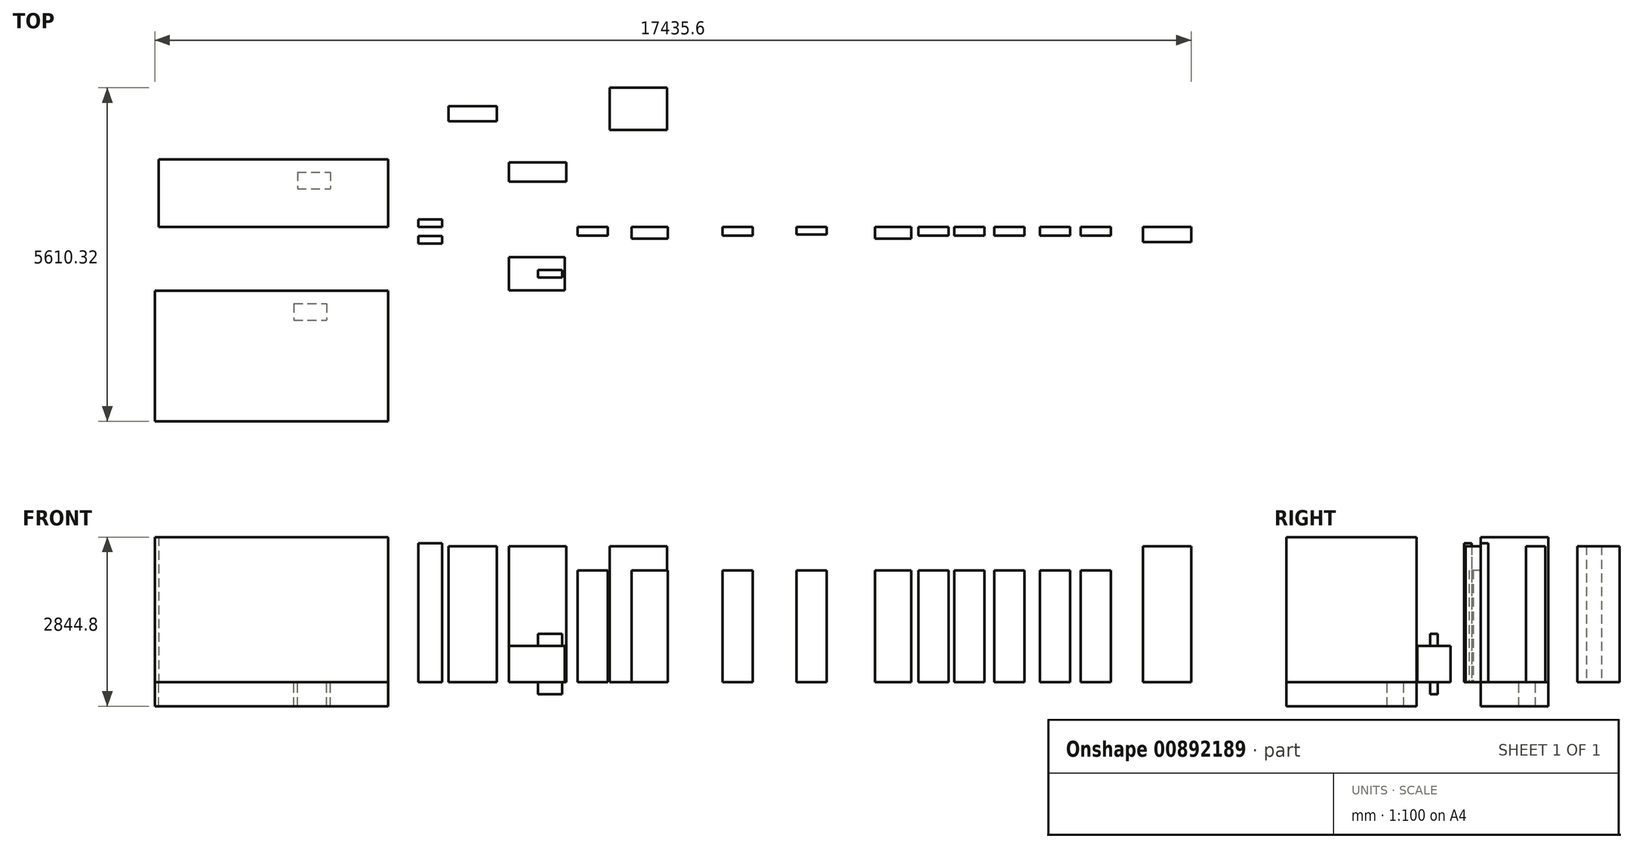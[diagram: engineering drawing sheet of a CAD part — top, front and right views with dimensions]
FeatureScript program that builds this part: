
annotation { "Feature Type Name" : "Feature", "Feature Type Description" : "" }
export const myFeature = defineFeature(function(context is Context, id is Id, definition is map)
    precondition{}
    {
        {
            var Q0;
            Q0=qCreatedBy(makeId("Top.planeOp"),FACE);
            var sketch = newSketch(context, id + "F0", { "sketchPlane" : qUnion([Q0])});
            skLineSegment(sketch, "E0.bottom", {"start": v(0, 0) * mm, "end": v(401.32, 0) * mm});
            skLineSegment(sketch, "E0.top", {"start": v(0, 127) * mm, "end": v(401.32, 127) * mm});
            skLineSegment(sketch, "E0.left", {"start": v(0, 0) * mm, "end": v(0, 127) * mm});
            skLineSegment(sketch, "E0.right", {"start": v(401.32, 0) * mm, "end": v(401.32, 127) * mm});
            skSolve(sketch);
        }
        {
            var Q0;
            Q0=makeQuery(id+"F0.imprint","IMPRINT",FACE,{"disambiguationData":[TD([[makeQuery(id+"F0.imprint","IMPRINT",EDGE,{"derivedFrom":sQuery(id+"F0.wireOp",EDGE,"E0.bottom")}),1.0]])]});
            extrude(context, id + "F1", {"entities" : qUnion([Q0]), "depth" : 2336.8 * mm, "offsetDistance" : 25.4 * mm});
        }
        {
            var Q0;
            Q0=qCreatedBy(makeId("Top.planeOp"),FACE);
            var sketch = newSketch(context, id + "F2", { "sketchPlane" : qUnion([Q0])});
            skLineSegment(sketch, "E1", {"start": v(0, 0) * mm, "end": v(-508, 0) * mm, "construction": true});
            skLineSegment(sketch, "E2.bottom", {"start": v(-508, 0) * mm, "end": v(-4369.82, 0) * mm});
            skLineSegment(sketch, "E2.top", {"start": v(-508, 1138.94) * mm, "end": v(-4369.82, 1138.94) * mm});
            skLineSegment(sketch, "E2.left", {"start": v(-508, 0) * mm, "end": v(-508, 1138.94) * mm});
            skLineSegment(sketch, "E2.right", {"start": v(-4369.82, 0) * mm, "end": v(-4369.82, 1138.94) * mm});
            skLineSegment(sketch, "E3", {"start": v(-4369.82, 1138.94) * mm, "end": v(-2033.02, 1138.94) * mm, "construction": true});
            skLineSegment(sketch, "E4", {"start": v(-2033.02, 1138.94) * mm, "end": v(-2033.02, 923.04) * mm, "construction": true});
            skLineSegment(sketch, "E5.bottom", {"start": v(-2033.02, 923.04) * mm, "end": v(-1479.3, 923.04) * mm});
            skLineSegment(sketch, "E5.top", {"start": v(-2033.02, 643.64) * mm, "end": v(-1479.3, 643.64) * mm});
            skLineSegment(sketch, "E5.left", {"start": v(-2033.02, 923.04) * mm, "end": v(-2033.02, 643.64) * mm});
            skLineSegment(sketch, "E5.right", {"start": v(-1479.3, 923.04) * mm, "end": v(-1479.3, 643.64) * mm});
            skSolve(sketch);
        }
        {
            var Q0;
            Q0=makeQuery(id+"F2.imprint","IMPRINT",FACE,{"disambiguationData":[TD([[makeQuery(id+"F2.imprint","IMPRINT",EDGE,{"derivedFrom":sQuery(id+"F2.wireOp",EDGE,"E2.bottom")}),-1.0]])]});
            extrude(context, id + "F3", {"entities" : qUnion([Q0]), "oppositeDirection" : true, "depth" : 406.4 * mm, "offsetDistance" : 25.4 * mm});
        }
        {
            var Q0;
            Q0=qCreatedBy(makeId("Top.planeOp"),FACE);
            var sketch = newSketch(context, id + "F4", { "sketchPlane" : qUnion([Q0])});
            skLineSegment(sketch, "E6", {"start": v(0, 0) * mm, "end": v(0, -1524) * mm, "construction": true});
            skLineSegment(sketch, "E7", {"start": v(0, -1524) * mm, "end": v(-508, -1524) * mm, "construction": true});
            skLineSegment(sketch, "E8", {"start": v(-508, -1524) * mm, "end": v(-508, -3269.23) * mm});
            skLineSegment(sketch, "E9", {"start": v(-508, -3269.23) * mm, "end": v(-4430.78, -3269.23) * mm});
            skLineSegment(sketch, "E10", {"start": v(-4430.78, -3269.23) * mm, "end": v(-4430.78, -1075.7) * mm});
            skLineSegment(sketch, "E11", {"start": v(-4430.78, -1075.7) * mm, "end": v(-2581.4, -1075.7) * mm});
            skLineSegment(sketch, "E12", {"start": v(-4430.78, -1075.7) * mm, "end": v(-2093.98, -1075.7) * mm, "construction": true});
            skLineSegment(sketch, "E13", {"start": v(-2093.98, -1075.7) * mm, "end": v(-2093.98, -1291.6) * mm, "construction": true});
            skLineSegment(sketch, "E14.bottom", {"start": v(-2093.98, -1291.6) * mm, "end": v(-1540.26, -1291.6) * mm});
            skLineSegment(sketch, "E14.top", {"start": v(-2093.98, -1571) * mm, "end": v(-1540.26, -1571) * mm});
            skLineSegment(sketch, "E14.left", {"start": v(-2093.98, -1291.6) * mm, "end": v(-2093.98, -1571) * mm});
            skLineSegment(sketch, "E14.right", {"start": v(-1540.26, -1291.6) * mm, "end": v(-1540.26, -1571) * mm});
            skLineSegment(sketch, "E15", {"start": v(-2581.4, -1075.7) * mm, "end": v(-508, -1075.7) * mm});
            skLineSegment(sketch, "E16", {"start": v(-508, -1075.7) * mm, "end": v(-508, -1524) * mm});
            skSolve(sketch);
        }
        {
            var Q0;
            Q0=makeQuery(id+"F4.imprint","IMPRINT",FACE,{"disambiguationData":[TD([[makeQuery(id+"F4.imprint","IMPRINT",EDGE,{"derivedFrom":sQuery(id+"F4.wireOp",EDGE,"E8")}),-1.0]])]});
            extrude(context, id + "F5", {"entities" : qUnion([Q0]), "oppositeDirection" : true, "depth" : 406.4 * mm, "offsetDistance" : 25.4 * mm});
        }
        {
            var Q0;
            Q0=qCreatedBy(makeId("Top.planeOp"),FACE);
            var sketch = newSketch(context, id + "F6", { "sketchPlane" : qUnion([Q0])});
            skLineSegment(sketch, "E17", {"start": v(0, 0) * mm, "end": v(0, -508) * mm, "construction": true});
            skLineSegment(sketch, "E18", {"start": v(0, -508) * mm, "end": v(1524, -508) * mm, "construction": true});
            skLineSegment(sketch, "E19.bottom", {"start": v(1524, -508) * mm, "end": v(2463.8, -508) * mm});
            skLineSegment(sketch, "E19.top", {"start": v(1524, -1066.8) * mm, "end": v(2463.8, -1066.8) * mm});
            skLineSegment(sketch, "E19.left", {"start": v(1524, -508) * mm, "end": v(1524, -1066.8) * mm});
            skLineSegment(sketch, "E19.right", {"start": v(2463.8, -508) * mm, "end": v(2463.8, -1066.8) * mm});
            skLineSegment(sketch, "E20", {"start": v(2463.8, -508) * mm, "end": v(2217.42, -508) * mm, "construction": true});
            skLineSegment(sketch, "E21", {"start": v(2217.42, -508) * mm, "end": v(2217.42, -787.4) * mm, "construction": true});
            skLineSegment(sketch, "E22.bottom", {"start": v(2418.08, -850.9) * mm, "end": v(2016.76, -850.9) * mm});
            skLineSegment(sketch, "E22.top", {"start": v(2418.08, -723.9) * mm, "end": v(2016.76, -723.9) * mm});
            skLineSegment(sketch, "E22.left", {"start": v(2418.08, -850.9) * mm, "end": v(2418.08, -723.9) * mm});
            skLineSegment(sketch, "E22.right", {"start": v(2016.76, -850.9) * mm, "end": v(2016.76, -723.9) * mm});
            skPoint(sketch, "E22.middle", {"position": v(2217.42, -787.4) * mm});
            skSolve(sketch);
        }
        {
            var Q0;
            Q0=makeQuery(id+"F6.imprint","IMPRINT",FACE,{"disambiguationData":[TD([[makeQuery(id+"F6.imprint","IMPRINT",EDGE,{"derivedFrom":sQuery(id+"F6.wireOp",EDGE,"E19.bottom")}),-1.0]])]});
            var Q1;
            Q1=makeQuery(id+"F6.imprint","IMPRINT",FACE,{"disambiguationData":[TD([[makeQuery(id+"F6.imprint","IMPRINT",EDGE,{"derivedFrom":sQuery(id+"F6.wireOp",EDGE,"E22.bottom")}),-1.0]])]});
            extrude(context, id + "F7", {"entities" : qUnion([Q0, Q1]), "depth" : 609.6 * mm, "offsetDistance" : 25.4 * mm});
        }
        {
            var Q0;
            Q0=makeQuery(id+"F6.imprint","IMPRINT",FACE,{"disambiguationData":[TD([[makeQuery(id+"F6.imprint","IMPRINT",EDGE,{"derivedFrom":sQuery(id+"F6.wireOp",EDGE,"E22.bottom")}),-1.0]])]});
            extrude(context, id + "F8", {"entities" : qUnion([Q0]), "operationType" : NewBodyOperationType.ADD, "oppositeDirection" : true, "depth" : 203.2 * mm, "offsetDistance" : 25.4 * mm});
        }
        {
            var Q0;
            Q0=makeQuery(id+"F7.opExtrude","CAP_FACE",FACE,{"disambiguationData":[OSD([sQuery(id+"F6.wireOp",EDGE,"E19.bottom"),sQuery(id+"F6.wireOp",EDGE,"E19.top"),sQuery(id+"F6.wireOp",EDGE,"E19.left"),sQuery(id+"F6.wireOp",EDGE,"E19.right")])],"isStart":false});
            var sketch = newSketch(context, id + "F9", { "sketchPlane" : qUnion([Q0])});
            skLineSegment(sketch, "E23", {"start": v(2463.8, -787.4) * mm, "end": v(2217.42, -787.4) * mm, "construction": true});
            skLineSegment(sketch, "E24.bottom", {"start": v(2418.08, -850.9) * mm, "end": v(2016.76, -850.9) * mm});
            skLineSegment(sketch, "E24.top", {"start": v(2418.08, -723.9) * mm, "end": v(2016.76, -723.9) * mm});
            skLineSegment(sketch, "E24.left", {"start": v(2418.08, -850.9) * mm, "end": v(2418.08, -723.9) * mm});
            skLineSegment(sketch, "E24.right", {"start": v(2016.76, -850.9) * mm, "end": v(2016.76, -723.9) * mm});
            skPoint(sketch, "E24.middle", {"position": v(2217.42, -787.4) * mm});
            skSolve(sketch);
        }
        {
            var Q0;
            Q0=makeQuery(id+"F9.imprint","IMPRINT",FACE,{"disambiguationData":[TD([[makeQuery(id+"F9.imprint","IMPRINT",EDGE,{"derivedFrom":sQuery(id+"F9.wireOp",EDGE,"E24.bottom")}),-1.0]])]});
            extrude(context, id + "F10", {"entities" : qUnion([Q0]), "operationType" : NewBodyOperationType.ADD, "depth" : 203.2 * mm, "offsetDistance" : 25.4 * mm});
        }
        {
            var Q0;
            Q0=makeQuery(id+"F2.imprint","IMPRINT",FACE,{"disambiguationData":[TD([[makeQuery(id+"F2.imprint","IMPRINT",EDGE,{"derivedFrom":sQuery(id+"F2.wireOp",EDGE,"E2.bottom")}),-1.0]])]});
            var Q1;
            Q1=makeQuery(id+"F2.imprint","IMPRINT",FACE,{"disambiguationData":[TD([[makeQuery(id+"F2.imprint","IMPRINT",EDGE,{"derivedFrom":sQuery(id+"F2.wireOp",EDGE,"E5.bottom")}),-1.0]])]});
            extrude(context, id + "F11", {"entities" : qUnion([Q0, Q1]), "depth" : 2438.4 * mm, "offsetDistance" : 25.4 * mm});
        }
        {
            var Q0;
            Q0=makeQuery(id+"F4.imprint","IMPRINT",FACE,{"disambiguationData":[TD([[makeQuery(id+"F4.imprint","IMPRINT",EDGE,{"derivedFrom":sQuery(id+"F4.wireOp",EDGE,"E14.bottom")}),-1.0]])]});
            var Q1;
            Q1=makeQuery(id+"F4.imprint","IMPRINT",FACE,{"disambiguationData":[TD([[makeQuery(id+"F4.imprint","IMPRINT",EDGE,{"derivedFrom":sQuery(id+"F4.wireOp",EDGE,"E8")}),-1.0]])]});
            extrude(context, id + "F12", {"entities" : qUnion([Q0, Q1]), "depth" : 2438.4 * mm, "offsetDistance" : 25.4 * mm});
        }
        {
            var Q0;
            Q0=qCreatedBy(makeId("Top.planeOp"),FACE);
            var sketch = newSketch(context, id + "F13", { "sketchPlane" : qUnion([Q0])});
            skLineSegment(sketch, "E25", {"start": v(0, 0) * mm, "end": v(0, 762) * mm, "construction": true});
            skLineSegment(sketch, "E26", {"start": v(0, 762) * mm, "end": v(1524, 762) * mm, "construction": true});
            skLineSegment(sketch, "E27.bottom", {"start": v(1524, 762) * mm, "end": v(2489.2, 762) * mm});
            skLineSegment(sketch, "E27.top", {"start": v(1524, 1085.85) * mm, "end": v(2489.2, 1085.85) * mm});
            skLineSegment(sketch, "E27.left", {"start": v(1524, 762) * mm, "end": v(1524, 1085.85) * mm});
            skLineSegment(sketch, "E27.right", {"start": v(2489.2, 762) * mm, "end": v(2489.2, 1085.85) * mm});
            skSolve(sketch);
        }
        {
            var Q0;
            Q0=makeQuery(id+"F13.imprint","IMPRINT",FACE,{"disambiguationData":[TD([[makeQuery(id+"F13.imprint","IMPRINT",EDGE,{"derivedFrom":sQuery(id+"F13.wireOp",EDGE,"E27.bottom")}),1.0]])]});
            extrude(context, id + "F14", {"entities" : qUnion([Q0]), "depth" : 2286 * mm, "offsetDistance" : 25.4 * mm});
        }
        {
            var Q0;
            Q0=qCreatedBy(makeId("Top.planeOp"),FACE);
            var sketch = newSketch(context, id + "F15", { "sketchPlane" : qUnion([Q0])});
            skLineSegment(sketch, "E28", {"start": v(0, 0) * mm, "end": v(0, 2032) * mm, "construction": true});
            skLineSegment(sketch, "E29", {"start": v(0, 2032) * mm, "end": v(508, 2032) * mm, "construction": true});
            skLineSegment(sketch, "E30.bottom", {"start": v(508, 2032) * mm, "end": v(1320.8, 2032) * mm});
            skLineSegment(sketch, "E30.top", {"start": v(508, 1778) * mm, "end": v(1320.8, 1778) * mm});
            skLineSegment(sketch, "E30.left", {"start": v(508, 2032) * mm, "end": v(508, 1778) * mm});
            skLineSegment(sketch, "E30.right", {"start": v(1320.8, 2032) * mm, "end": v(1320.8, 1778) * mm});
            skSolve(sketch);
        }
        {
            var Q0;
            Q0=makeQuery(id+"F15.imprint","IMPRINT",FACE,{"disambiguationData":[TD([[makeQuery(id+"F15.imprint","IMPRINT",EDGE,{"derivedFrom":sQuery(id+"F15.wireOp",EDGE,"E30.bottom")}),-1.0]])]});
            extrude(context, id + "F16", {"entities" : qUnion([Q0]), "depth" : 2286 * mm, "offsetDistance" : 25.4 * mm});
        }
        {
            var Q0;
            Q0=qCreatedBy(makeId("Top.planeOp"),FACE);
            var sketch = newSketch(context, id + "F17", { "sketchPlane" : qUnion([Q0])});
            skLineSegment(sketch, "E31", {"start": v(0, 0) * mm, "end": v(3588.96, 0) * mm, "construction": true});
            skLineSegment(sketch, "E32.bottom", {"start": v(3588.96, 0) * mm, "end": v(4198.56, 0) * mm});
            skLineSegment(sketch, "E32.top", {"start": v(3588.96, -196.85) * mm, "end": v(4198.56, -196.85) * mm});
            skLineSegment(sketch, "E32.left", {"start": v(3588.96, 0) * mm, "end": v(3588.96, -196.85) * mm});
            skLineSegment(sketch, "E32.right", {"start": v(4198.56, 0) * mm, "end": v(4198.56, -196.85) * mm});
            skSolve(sketch);
        }
        {
            var Q0;
            Q0=makeQuery(id+"F17.imprint","IMPRINT",FACE,{"disambiguationData":[TD([[makeQuery(id+"F17.imprint","IMPRINT",EDGE,{"derivedFrom":sQuery(id+"F17.wireOp",EDGE,"E32.bottom")}),-1.0]])]});
            extrude(context, id + "F18", {"entities" : qUnion([Q0]), "depth" : 1879.6 * mm, "offsetDistance" : 25.4 * mm});
        }
        {
            var Q0;
            Q0=qCreatedBy(makeId("Top.planeOp"),FACE);
            var sketch = newSketch(context, id + "F19", { "sketchPlane" : qUnion([Q0])});
            skLineSegment(sketch, "E33", {"start": v(0, 0) * mm, "end": v(0, -152.4) * mm, "construction": true});
            skLineSegment(sketch, "E34.bottom", {"start": v(0, -152.4) * mm, "end": v(401.32, -152.4) * mm});
            skLineSegment(sketch, "E34.top", {"start": v(0, -279.4) * mm, "end": v(401.32, -279.4) * mm});
            skLineSegment(sketch, "E34.left", {"start": v(0, -152.4) * mm, "end": v(0, -279.4) * mm});
            skLineSegment(sketch, "E34.right", {"start": v(401.32, -152.4) * mm, "end": v(401.32, -279.4) * mm});
            skSolve(sketch);
        }
        {
            var Q0;
            Q0=makeQuery(id+"F19.imprint","IMPRINT",FACE,{"disambiguationData":[TD([[makeQuery(id+"F19.imprint","IMPRINT",EDGE,{"derivedFrom":sQuery(id+"F19.wireOp",EDGE,"E34.bottom")}),-1.0]])]});
            extrude(context, id + "F20", {"entities" : qUnion([Q0]), "depth" : 2336.8 * mm, "offsetDistance" : 25.4 * mm});
        }
        {
            var Q0;
            Q0=qCreatedBy(makeId("Top.planeOp"),FACE);
            var sketch = newSketch(context, id + "F21", { "sketchPlane" : qUnion([Q0])});
            skLineSegment(sketch, "E35", {"start": v(0, 0) * mm, "end": v(3219.45, 0) * mm, "construction": true});
            skLineSegment(sketch, "E36", {"start": v(3219.45, 0) * mm, "end": v(3219.45, 1629.9) * mm, "construction": true});
            skLineSegment(sketch, "E37.bottom", {"start": v(3219.45, 1629.9) * mm, "end": v(4184.65, 1629.9) * mm});
            skLineSegment(sketch, "E37.top", {"start": v(3219.45, 2341.1) * mm, "end": v(4184.65, 2341.1) * mm});
            skLineSegment(sketch, "E37.left", {"start": v(3219.45, 1629.9) * mm, "end": v(3219.45, 2341.1) * mm});
            skLineSegment(sketch, "E37.right", {"start": v(4184.65, 1629.9) * mm, "end": v(4184.65, 2341.1) * mm});
            skSolve(sketch);
        }
        {
            var Q0;
            Q0=makeQuery(id+"F21.imprint","IMPRINT",FACE,{"disambiguationData":[TD([[makeQuery(id+"F21.imprint","IMPRINT",EDGE,{"derivedFrom":sQuery(id+"F21.wireOp",EDGE,"E37.bottom")}),1.0]])]});
            extrude(context, id + "F22", {"entities" : qUnion([Q0]), "depth" : 2286 * mm, "offsetDistance" : 25.4 * mm});
        }
        {
            var Q0;
            Q0=qCreatedBy(makeId("Top.planeOp"),FACE);
            var sketch = newSketch(context, id + "F23", { "sketchPlane" : qUnion([Q0])});
            skLineSegment(sketch, "E38", {"start": v(0, 0) * mm, "end": v(2681.18, 0) * mm, "construction": true});
            skLineSegment(sketch, "E39.bottom", {"start": v(2681.18, 0) * mm, "end": v(3189.18, 0) * mm});
            skLineSegment(sketch, "E39.top", {"start": v(2681.18, -146.05) * mm, "end": v(3189.18, -146.05) * mm});
            skLineSegment(sketch, "E39.left", {"start": v(2681.18, 0) * mm, "end": v(2681.18, -146.05) * mm});
            skLineSegment(sketch, "E39.right", {"start": v(3189.18, 0) * mm, "end": v(3189.18, -146.05) * mm});
            skSolve(sketch);
        }
        {
            var Q0;
            Q0=makeQuery(id+"F23.imprint","IMPRINT",FACE,{"disambiguationData":[TD([[makeQuery(id+"F23.imprint","IMPRINT",EDGE,{"derivedFrom":sQuery(id+"F23.wireOp",EDGE,"E39.bottom")}),-1.0]])]});
            extrude(context, id + "F24", {"entities" : qUnion([Q0]), "depth" : 1879.6 * mm, "offsetDistance" : 25.4 * mm});
        }
        {
            var Q0;
            Q0=makeQuery(id+"F24.opExtrude","SWEPT_BODY",BODY,{"disambiguationData":[OSD([sQuery(id+"F23.wireOp",EDGE,"E39.bottom"),sQuery(id+"F23.wireOp",EDGE,"E39.top"),sQuery(id+"F23.wireOp",EDGE,"E39.left"),sQuery(id+"F23.wireOp",EDGE,"E39.right")])]});
            transform(context, id + "F25", {"entities" : qUnion([Q0]), "transformType" : TransformType.TRANSLATION_3D, "dx" : 2438.4 * mm, "dy" : 0 * mm, "dz" : 0 * mm, "makeCopy" : true});
        }
        {
            var Q0;
            Q0=qCreatedBy(makeId("Top.planeOp"),FACE);
            var sketch = newSketch(context, id + "F26", { "sketchPlane" : qUnion([Q0])});
            skLineSegment(sketch, "E40", {"start": v(0, 0) * mm, "end": v(6364.64, 0) * mm, "construction": true});
            skLineSegment(sketch, "E41.bottom", {"start": v(6364.64, 0) * mm, "end": v(6872.64, 0) * mm});
            skLineSegment(sketch, "E41.top", {"start": v(6364.64, -127) * mm, "end": v(6872.64, -127) * mm});
            skLineSegment(sketch, "E41.left", {"start": v(6364.64, 0) * mm, "end": v(6364.64, -127) * mm});
            skLineSegment(sketch, "E41.right", {"start": v(6872.64, 0) * mm, "end": v(6872.64, -127) * mm});
            skSolve(sketch);
        }
        {
            var Q0;
            Q0=makeQuery(id+"F26.imprint","IMPRINT",FACE,{"disambiguationData":[TD([[makeQuery(id+"F26.imprint","IMPRINT",EDGE,{"derivedFrom":sQuery(id+"F26.wireOp",EDGE,"E41.bottom")}),-1.0]])]});
            extrude(context, id + "F27", {"entities" : qUnion([Q0]), "depth" : 1879.6 * mm, "offsetDistance" : 25.4 * mm});
        }
        {
            var Q0;
            Q0=qCreatedBy(makeId("Top.planeOp"),FACE);
            var sketch = newSketch(context, id + "F28", { "sketchPlane" : qUnion([Q0])});
            skLineSegment(sketch, "E42", {"start": v(0, 0) * mm, "end": v(7683, 0) * mm, "construction": true});
            skLineSegment(sketch, "E43.bottom", {"start": v(7683, 0) * mm, "end": v(8292.6, 0) * mm});
            skLineSegment(sketch, "E43.top", {"start": v(7683, -196.85) * mm, "end": v(8292.6, -196.85) * mm});
            skLineSegment(sketch, "E43.left", {"start": v(7683, 0) * mm, "end": v(7683, -196.85) * mm});
            skLineSegment(sketch, "E43.right", {"start": v(8292.6, 0) * mm, "end": v(8292.6, -196.85) * mm});
            skSolve(sketch);
        }
        {
            var Q0;
            Q0=makeQuery(id+"F28.imprint","IMPRINT",FACE,{"disambiguationData":[TD([[makeQuery(id+"F28.imprint","IMPRINT",EDGE,{"derivedFrom":sQuery(id+"F28.wireOp",EDGE,"E43.bottom")}),-1.0]])]});
            extrude(context, id + "F29", {"entities" : qUnion([Q0]), "depth" : 1879.6 * mm, "offsetDistance" : 25.4 * mm});
        }
        {
            var Q0;
            Q0=qCreatedBy(makeId("Top.planeOp"),FACE);
            var sketch = newSketch(context, id + "F30", { "sketchPlane" : qUnion([Q0])});
            skLineSegment(sketch, "E44", {"start": v(0, 0) * mm, "end": v(8414.26, 0) * mm, "construction": true});
            skLineSegment(sketch, "E45.bottom", {"start": v(8414.26, 0) * mm, "end": v(8922.26, 0) * mm});
            skLineSegment(sketch, "E45.top", {"start": v(8414.26, -146.05) * mm, "end": v(8922.26, -146.05) * mm});
            skLineSegment(sketch, "E45.left", {"start": v(8414.26, 0) * mm, "end": v(8414.26, -146.05) * mm});
            skLineSegment(sketch, "E45.right", {"start": v(8922.26, 0) * mm, "end": v(8922.26, -146.05) * mm});
            skSolve(sketch);
        }
        {
            var Q0;
            Q0=makeQuery(id+"F30.imprint","IMPRINT",FACE,{"disambiguationData":[TD([[makeQuery(id+"F30.imprint","IMPRINT",EDGE,{"derivedFrom":sQuery(id+"F30.wireOp",EDGE,"E45.bottom")}),-1.0]])]});
            extrude(context, id + "F31", {"entities" : qUnion([Q0]), "depth" : 1879.6 * mm, "offsetDistance" : 25.4 * mm});
        }
        {
            var Q0;
            Q0=qCreatedBy(makeId("Top.planeOp"),FACE);
            var sketch = newSketch(context, id + "F32", { "sketchPlane" : qUnion([Q0])});
            skLineSegment(sketch, "E46", {"start": v(0, 0) * mm, "end": v(9020.03, 0) * mm, "construction": true});
            skLineSegment(sketch, "E47.bottom", {"start": v(9020.03, 0) * mm, "end": v(9528.03, 0) * mm});
            skLineSegment(sketch, "E47.top", {"start": v(9020.03, -146.05) * mm, "end": v(9528.03, -146.05) * mm});
            skLineSegment(sketch, "E47.left", {"start": v(9020.03, 0) * mm, "end": v(9020.03, -146.05) * mm});
            skLineSegment(sketch, "E47.right", {"start": v(9528.03, 0) * mm, "end": v(9528.03, -146.05) * mm});
            skLineSegment(sketch, "E48", {"start": v(9020.03, 0) * mm, "end": v(9690.94, 0) * mm, "construction": true});
            skLineSegment(sketch, "E49.bottom", {"start": v(9690.94, 0) * mm, "end": v(10198.94, 0) * mm});
            skLineSegment(sketch, "E49.top", {"start": v(9690.94, -146.05) * mm, "end": v(10198.94, -146.05) * mm});
            skLineSegment(sketch, "E49.left", {"start": v(9690.94, 0) * mm, "end": v(9690.94, -146.05) * mm});
            skLineSegment(sketch, "E49.right", {"start": v(10198.94, 0) * mm, "end": v(10198.94, -146.05) * mm});
            skLineSegment(sketch, "E50", {"start": v(9690.94, 0) * mm, "end": v(10460.14, 0) * mm, "construction": true});
            skLineSegment(sketch, "E51.bottom", {"start": v(10460.14, 0) * mm, "end": v(10968.14, 0) * mm});
            skLineSegment(sketch, "E51.top", {"start": v(10460.14, -146.05) * mm, "end": v(10968.14, -146.05) * mm});
            skLineSegment(sketch, "E51.left", {"start": v(10460.14, 0) * mm, "end": v(10460.14, -146.05) * mm});
            skLineSegment(sketch, "E51.right", {"start": v(10968.14, 0) * mm, "end": v(10968.14, -146.05) * mm});
            skLineSegment(sketch, "E52", {"start": v(10460.14, 0) * mm, "end": v(11143.88, 0) * mm, "construction": true});
            skLineSegment(sketch, "E53.bottom", {"start": v(11143.88, 0) * mm, "end": v(11651.88, 0) * mm});
            skLineSegment(sketch, "E53.top", {"start": v(11143.88, -146.05) * mm, "end": v(11651.88, -146.05) * mm});
            skLineSegment(sketch, "E53.left", {"start": v(11143.88, 0) * mm, "end": v(11143.88, -146.05) * mm});
            skLineSegment(sketch, "E53.right", {"start": v(11651.88, 0) * mm, "end": v(11651.88, -146.05) * mm});
            skSolve(sketch);
        }
        {
            var Q0;
            Q0=makeQuery(id+"F32.imprint","IMPRINT",FACE,{"disambiguationData":[TD([[makeQuery(id+"F32.imprint","IMPRINT",EDGE,{"derivedFrom":sQuery(id+"F32.wireOp",EDGE,"E47.bottom")}),-1.0]])]});
            var Q1;
            Q1=makeQuery(id+"F32.imprint","IMPRINT",FACE,{"disambiguationData":[TD([[makeQuery(id+"F32.imprint","IMPRINT",EDGE,{"derivedFrom":sQuery(id+"F32.wireOp",EDGE,"E49.bottom")}),-1.0]])]});
            var Q2;
            Q2=makeQuery(id+"F32.imprint","IMPRINT",FACE,{"disambiguationData":[TD([[makeQuery(id+"F32.imprint","IMPRINT",EDGE,{"derivedFrom":sQuery(id+"F32.wireOp",EDGE,"E51.bottom")}),-1.0]])]});
            var Q3;
            Q3=makeQuery(id+"F32.imprint","IMPRINT",FACE,{"disambiguationData":[TD([[makeQuery(id+"F32.imprint","IMPRINT",EDGE,{"derivedFrom":sQuery(id+"F32.wireOp",EDGE,"E53.bottom")}),-1.0]])]});
            extrude(context, id + "F33", {"entities" : qUnion([Q0, Q1, Q2, Q3]), "depth" : 1879.6 * mm, "offsetDistance" : 25.4 * mm});
        }
        {
            var Q0;
            Q0=qCreatedBy(makeId("Top.planeOp"),FACE);
            var sketch = newSketch(context, id + "F34", { "sketchPlane" : qUnion([Q0])});
            skLineSegment(sketch, "E54", {"start": v(0, 0) * mm, "end": v(12192, 0) * mm, "construction": true});
            skLineSegment(sketch, "E55.bottom", {"start": v(12192, 0) * mm, "end": v(13004.8, 0) * mm});
            skLineSegment(sketch, "E55.top", {"start": v(12192, -254) * mm, "end": v(13004.8, -254) * mm});
            skLineSegment(sketch, "E55.left", {"start": v(12192, 0) * mm, "end": v(12192, -254) * mm});
            skLineSegment(sketch, "E55.right", {"start": v(13004.8, 0) * mm, "end": v(13004.8, -254) * mm});
            skSolve(sketch);
        }
        {
            var Q0;
            Q0=makeQuery(id+"F34.imprint","IMPRINT",FACE,{"disambiguationData":[TD([[makeQuery(id+"F34.imprint","IMPRINT",EDGE,{"derivedFrom":sQuery(id+"F34.wireOp",EDGE,"E55.bottom")}),-1.0]])]});
            extrude(context, id + "F35", {"entities" : qUnion([Q0]), "depth" : 2286 * mm, "offsetDistance" : 25.4 * mm});
        }
    });
